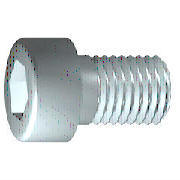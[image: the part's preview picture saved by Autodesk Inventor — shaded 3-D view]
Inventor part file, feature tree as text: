
AUTODESK INVENTOR PART (.ipt)
format: ipt  version: 2023.5 (Build 275446000, 446)  size: 185,856 bytes
history: native  units: mm (DEFAULTED — no unit token found)
features: extrude x1, plane x1, fillet x1
ambient origin geometry x7: Origin, YZ Plane, XY Plane, X Axis, Y Axis, Z Axis, Center Point
bodies: Solid1 (feature_tree), Body (feature_tree)
feature tree (3):
  extrude  "Slot"  Depth=25.4mm
  plane  "Work Plane1"
  fillet  "Fillet2"  Radius=2.5401mm
